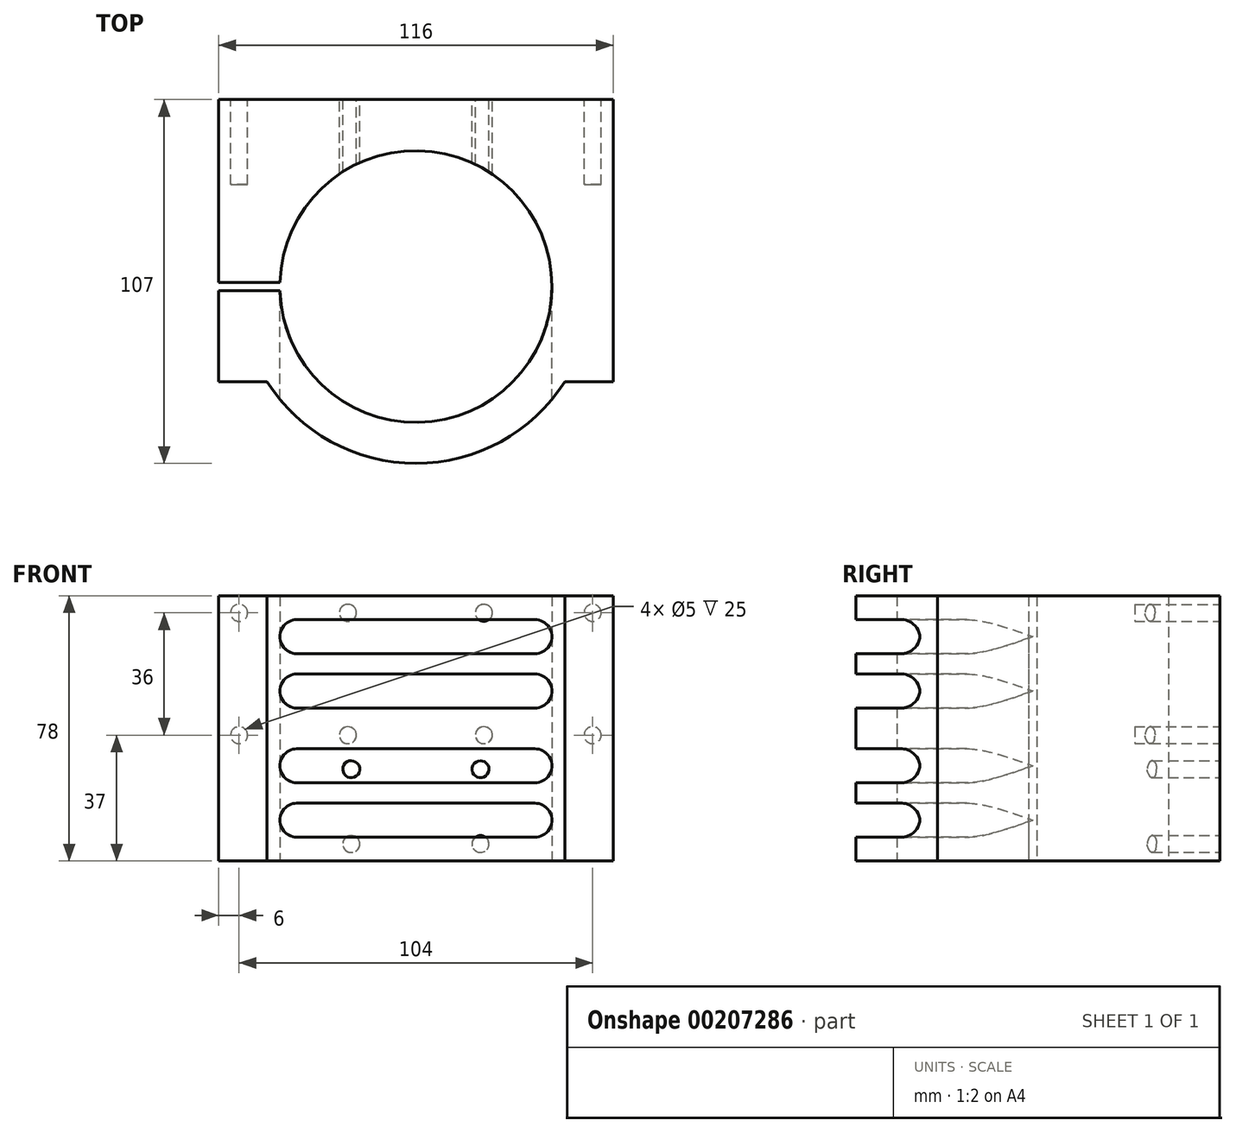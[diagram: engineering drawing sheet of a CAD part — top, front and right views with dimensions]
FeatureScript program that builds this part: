
annotation { "Feature Type Name" : "Feature", "Feature Type Description" : "" }
export const myFeature = defineFeature(function(context is Context, id is Id, definition is map)
    precondition{}
    {
        {
            var Q0;
            Q0=qCreatedBy(makeId("Top.planeOp"),FACE);
            var sketch = newSketch(context, id + "F0", { "sketchPlane" : qUnion([Q0])});
            skArc(sketch, "E0", {"start": v(-39.98, -1.25) * mm, "mid": v(40, 0) * mm, "end": v(-39.98, 1.25) * mm});
            skArc(sketch, "E1", {"start": v(-43.82, -28) * mm, "mid": v(0, -52) * mm, "end": v(43.82, -28) * mm});
            skLineSegment(sketch, "E2", {"start": v(-75, 55) * mm, "end": v(75, 55) * mm});
            skLineSegment(sketch, "E3", {"start": v(75, 55) * mm, "end": v(75, 41.5) * mm});
            skLineSegment(sketch, "E4", {"start": v(75, 41.5) * mm, "end": v(58, 41.5) * mm});
            skLineSegment(sketch, "E5", {"start": v(58, 41.5) * mm, "end": v(58, -28) * mm});
            skLineSegment(sketch, "E6", {"start": v(58, -28) * mm, "end": v(43.82, -28) * mm});
            skLineSegment(sketch, "E7", {"start": v(-58, -28) * mm, "end": v(-58, -1.25) * mm});
            skLineSegment(sketch, "E8", {"start": v(-58, 41.5) * mm, "end": v(-75, 41.5) * mm});
            skLineSegment(sketch, "E9", {"start": v(-75, 41.5) * mm, "end": v(-75, 55) * mm});
            skLineSegment(sketch, "E10", {"start": v(0, 0) * mm, "end": v(0, 55) * mm, "construction": true});
            skLineSegment(sketch, "E11.trimOffspring", {"start": v(-43.82, -28) * mm, "end": v(-58, -28) * mm});
            skLineSegment(sketch, "E12", {"start": v(-58, 1.25) * mm, "end": v(-39.98, 1.25) * mm});
            skLineSegment(sketch, "E13", {"start": v(-58, -1.25) * mm, "end": v(-39.98, -1.25) * mm});
            skLineSegment(sketch, "E14.trimOffspring", {"start": v(-58, 1.25) * mm, "end": v(-58, 41.5) * mm});
            skLineSegment(sketch, "E15", {"start": v(-58, 1.25) * mm, "end": v(-58, -1.25) * mm, "construction": true});
            skLineSegment(sketch, "E16", {"start": v(-58, 0) * mm, "end": v(0, 0) * mm, "construction": true});
            skSolve(sketch);
        }
        {
            var Q0;
            Q0=qSketchRegion(id+"F0",true);
            extrude(context, id + "F1", {"entities" : qUnion([Q0]), "depth" : 78 * mm});
        }
        {
            var Q0;
            Q0=makeQuery(id+"F1.opExtrude","SWEPT_FACE",FACE,{"disambiguationData":[OSD([sQuery(id+"F0.wireOp",EDGE,"E4")])]});
            var sketch = newSketch(context, id + "F2", { "sketchPlane" : qUnion([Q0])});
            skLineSegment(sketch, "E17.bottom", {"start": v(-67, 69) * mm, "end": v(67, 69) * mm, "construction": true});
            skLineSegment(sketch, "E17.top", {"start": v(-67, 9) * mm, "end": v(67, 9) * mm, "construction": true});
            skLineSegment(sketch, "E17.left", {"start": v(-67, 69) * mm, "end": v(-67, 9) * mm, "construction": true});
            skLineSegment(sketch, "E17.right", {"start": v(67, 69) * mm, "end": v(67, 9) * mm, "construction": true});
            skLineSegment(sketch, "E18", {"start": v(0, 78) * mm, "end": v(0, 0) * mm, "construction": true});
            skLineSegment(sketch, "E19", {"start": v(-75, 39) * mm, "end": v(75, 39) * mm, "construction": true});
            skCircle(sketch, "E20", {"center": v(-67, 69) * mm, "radius": 4 * mm});
            skCircle(sketch, "E21", {"center": v(-67, 39) * mm, "radius": 4 * mm});
            skCircle(sketch, "E22", {"center": v(-67, 9) * mm, "radius": 4 * mm});
            skCircle(sketch, "E23", {"center": v(67, 9) * mm, "radius": 4 * mm});
            skCircle(sketch, "E24", {"center": v(67, 39) * mm, "radius": 4 * mm});
            skCircle(sketch, "E25", {"center": v(67, 69) * mm, "radius": 4 * mm});
            skSolve(sketch);
        }
        {
            var Q0;
            Q0=qSketchRegion(id+"F2",true);
            extrude(context, id + "F3", {"entities" : qUnion([Q0]), "operationType" : NewBodyOperationType.REMOVE, "endBound" : BoundingType.THROUGH_ALL, "oppositeDirection" : true, "depth" : 25 * mm});
        }
        {
            var Q0;
            Q0=makeQuery(id+"F1.opExtrude","CAP_FACE",FACE,{"disambiguationData":[OSD([sQuery(id+"F0.wireOp",EDGE,"E0"),sQuery(id+"F0.wireOp",EDGE,"E1"),sQuery(id+"F0.wireOp",EDGE,"E2"),sQuery(id+"F0.wireOp",EDGE,"E3"),sQuery(id+"F0.wireOp",EDGE,"E4"),sQuery(id+"F0.wireOp",EDGE,"E5"),sQuery(id+"F0.wireOp",EDGE,"E6"),sQuery(id+"F0.wireOp",EDGE,"E7"),sQuery(id+"F0.wireOp",EDGE,"E8"),sQuery(id+"F0.wireOp",EDGE,"E9"),sQuery(id+"F0.wireOp",EDGE,"E11.trimOffspring"),sQuery(id+"F0.wireOp",EDGE,"E12"),sQuery(id+"F0.wireOp",EDGE,"E13"),sQuery(id+"F0.wireOp",EDGE,"E14.trimOffspring")])],"isStart":false});
            var sketch = newSketch(context, id + "F4", { "sketchPlane" : qUnion([Q0])});
            skLineSegment(sketch, "E26.bottom", {"start": v(-58, 41.5) * mm, "end": v(-75, 41.5) * mm});
            skLineSegment(sketch, "E26.top", {"start": v(-58, 55) * mm, "end": v(-75, 55) * mm});
            skLineSegment(sketch, "E26.left", {"start": v(-58, 41.5) * mm, "end": v(-58, 55) * mm});
            skLineSegment(sketch, "E26.right", {"start": v(-75, 41.5) * mm, "end": v(-75, 55) * mm});
            skLineSegment(sketch, "E27.bottom", {"start": v(58, 41.5) * mm, "end": v(75, 41.5) * mm});
            skLineSegment(sketch, "E27.top", {"start": v(58, 55) * mm, "end": v(75, 55) * mm});
            skLineSegment(sketch, "E27.left", {"start": v(58, 41.5) * mm, "end": v(58, 55) * mm});
            skLineSegment(sketch, "E27.right", {"start": v(75, 41.5) * mm, "end": v(75, 55) * mm});
            skSolve(sketch);
        }
        {
            var Q0;
            Q0 = qSketchRegion(id + "F4", true);
            extrude(context, id + "F5", {"entities" : qUnion([Q0]), "operationType" : NewBodyOperationType.REMOVE, "endBound" : BoundingType.THROUGH_ALL, "oppositeDirection" : true, "depth" : 25 * mm});
        }
        {
            var Q0;
            Q0=qCreatedBy(makeId("Front.planeOp"),FACE);
            var sketch = newSketch(context, id + "F6", { "sketchPlane" : qUnion([Q0])});
            skLineSegment(sketch, "E28", {"start": v(-35, 66) * mm, "end": v(35, 66) * mm, "construction": true});
            skLineSegment(sketch, "E29", {"start": v(-35, 50) * mm, "end": v(35, 50) * mm, "construction": true});
            skLineSegment(sketch, "E30", {"start": v(-35, 12) * mm, "end": v(35, 12) * mm, "construction": true});
            skLineSegment(sketch, "E31", {"start": v(0, 0) * mm, "end": v(0, 83.27) * mm, "construction": true});
            skArc(sketch, "E32.0.startCap", {"start": v(-35, 61) * mm, "mid": v(-40, 66) * mm, "end": v(-35, 71) * mm});
            skArc(sketch, "E32.0.endCap", {"start": v(35, 71) * mm, "mid": v(40, 66) * mm, "end": v(35, 61) * mm});
            skLineSegment(sketch, "E32.0.left", {"start": v(-35, 71) * mm, "end": v(35, 71) * mm});
            skLineSegment(sketch, "E32.0.right", {"start": v(-35, 61) * mm, "end": v(35, 61) * mm});
            skArc(sketch, "E32.1.startCap", {"start": v(-35, 45) * mm, "mid": v(-40, 50) * mm, "end": v(-35, 55) * mm});
            skArc(sketch, "E32.1.endCap", {"start": v(35, 55) * mm, "mid": v(40, 50) * mm, "end": v(35, 45) * mm});
            skLineSegment(sketch, "E32.1.left", {"start": v(-35, 55) * mm, "end": v(35, 55) * mm});
            skLineSegment(sketch, "E32.1.right", {"start": v(-35, 45) * mm, "end": v(35, 45) * mm});
            skArc(sketch, "E32.2.startCap", {"start": v(-35, 7) * mm, "mid": v(-40, 12) * mm, "end": v(-35, 17) * mm});
            skArc(sketch, "E32.2.endCap", {"start": v(35, 17) * mm, "mid": v(40, 12) * mm, "end": v(35, 7) * mm});
            skLineSegment(sketch, "E32.2.left", {"start": v(-35, 17) * mm, "end": v(35, 17) * mm});
            skLineSegment(sketch, "E32.2.right", {"start": v(-35, 7) * mm, "end": v(35, 7) * mm});
            skLineSegment(sketch, "E33", {"start": v(-35, 28) * mm, "end": v(35, 28) * mm, "construction": true});
            skArc(sketch, "E34.0.startCap", {"start": v(-35, 23) * mm, "mid": v(-40, 28) * mm, "end": v(-35, 33) * mm});
            skArc(sketch, "E34.0.endCap", {"start": v(35, 33) * mm, "mid": v(40, 28) * mm, "end": v(35, 23) * mm});
            skLineSegment(sketch, "E34.0.left", {"start": v(-35, 33) * mm, "end": v(35, 33) * mm});
            skLineSegment(sketch, "E34.0.right", {"start": v(-35, 23) * mm, "end": v(35, 23) * mm});
            skSolve(sketch);
        }
        {
            var Q0;
            Q0 = qSketchRegion(id + "F6", true);
            extrude(context, id + "F7", {"entities" : qUnion([Q0]), "operationType" : NewBodyOperationType.REMOVE, "endBound" : BoundingType.THROUGH_ALL, "depth" : 25 * mm});
        }
        {
            var Q0;
            Q0=makeQuery(id+"F1.opExtrude","SWEPT_FACE",FACE,{"disambiguationData":[OSD([sQuery(id+"F0.wireOp",EDGE,"E2")])]});
            var sketch = newSketch(context, id + "F8", { "sketchPlane" : qUnion([Q0])});
            skLineSegment(sketch, "E35", {"start": v(0, 0) * mm, "end": v(0, 78) * mm});
            skPoint(sketch, "E35.endSnap0", {"position": v(0, 78) * mm});
            skLineSegment(sketch, "E36.bottom", {"start": v(-52, 73) * mm, "end": v(-20, 73) * mm, "construction": true});
            skLineSegment(sketch, "E36.top", {"start": v(-52, 37) * mm, "end": v(-20, 37) * mm, "construction": true});
            skLineSegment(sketch, "E36.left", {"start": v(-52, 73) * mm, "end": v(-52, 37) * mm, "construction": true});
            skLineSegment(sketch, "E36.right", {"start": v(-20, 73) * mm, "end": v(-20, 37) * mm, "construction": true});
            skLineSegment(sketch, "E37.bottom", {"start": v(20, 73) * mm, "end": v(52, 73) * mm, "construction": true});
            skLineSegment(sketch, "E37.top", {"start": v(20, 37) * mm, "end": v(52, 37) * mm, "construction": true});
            skLineSegment(sketch, "E37.left", {"start": v(20, 73) * mm, "end": v(20, 37) * mm, "construction": true});
            skLineSegment(sketch, "E37.right", {"start": v(52, 73) * mm, "end": v(52, 37) * mm, "construction": true});
            skCircle(sketch, "E38", {"center": v(-52, 73) * mm, "radius": 2.5 * mm});
            skCircle(sketch, "E39", {"center": v(-20, 73) * mm, "radius": 2.5 * mm});
            skCircle(sketch, "E40", {"center": v(-20, 37) * mm, "radius": 2.5 * mm});
            skCircle(sketch, "E41", {"center": v(-52, 37) * mm, "radius": 2.5 * mm});
            skCircle(sketch, "E42", {"center": v(20, 73) * mm, "radius": 2.5 * mm});
            skCircle(sketch, "E43", {"center": v(20, 37) * mm, "radius": 2.5 * mm});
            skCircle(sketch, "E44", {"center": v(52, 37) * mm, "radius": 2.5 * mm});
            skCircle(sketch, "E45", {"center": v(52, 73) * mm, "radius": 2.5 * mm});
            skLineSegment(sketch, "E46.bottom", {"start": v(-19, 27) * mm, "end": v(19, 27) * mm, "construction": true});
            skLineSegment(sketch, "E46.top", {"start": v(-19, 5) * mm, "end": v(19, 5) * mm, "construction": true});
            skLineSegment(sketch, "E46.left", {"start": v(-19, 27) * mm, "end": v(-19, 5) * mm, "construction": true});
            skLineSegment(sketch, "E46.right", {"start": v(19, 27) * mm, "end": v(19, 5) * mm, "construction": true});
            skCircle(sketch, "E47", {"center": v(-19, 27) * mm, "radius": 2.5 * mm});
            skCircle(sketch, "E48", {"center": v(-19, 5) * mm, "radius": 2.5 * mm});
            skCircle(sketch, "E49", {"center": v(19, 5) * mm, "radius": 2.5 * mm});
            skCircle(sketch, "E50", {"center": v(19, 27) * mm, "radius": 2.5 * mm});
            skSolve(sketch);
        }
        {
            var Q0;
            Q0 = qSketchRegion(id + "F8", true);
            extrude(context, id + "F9", {"entities" : qUnion([Q0]), "operationType" : NewBodyOperationType.REMOVE, "oppositeDirection" : true, "depth" : 25 * mm});
        }
    });
